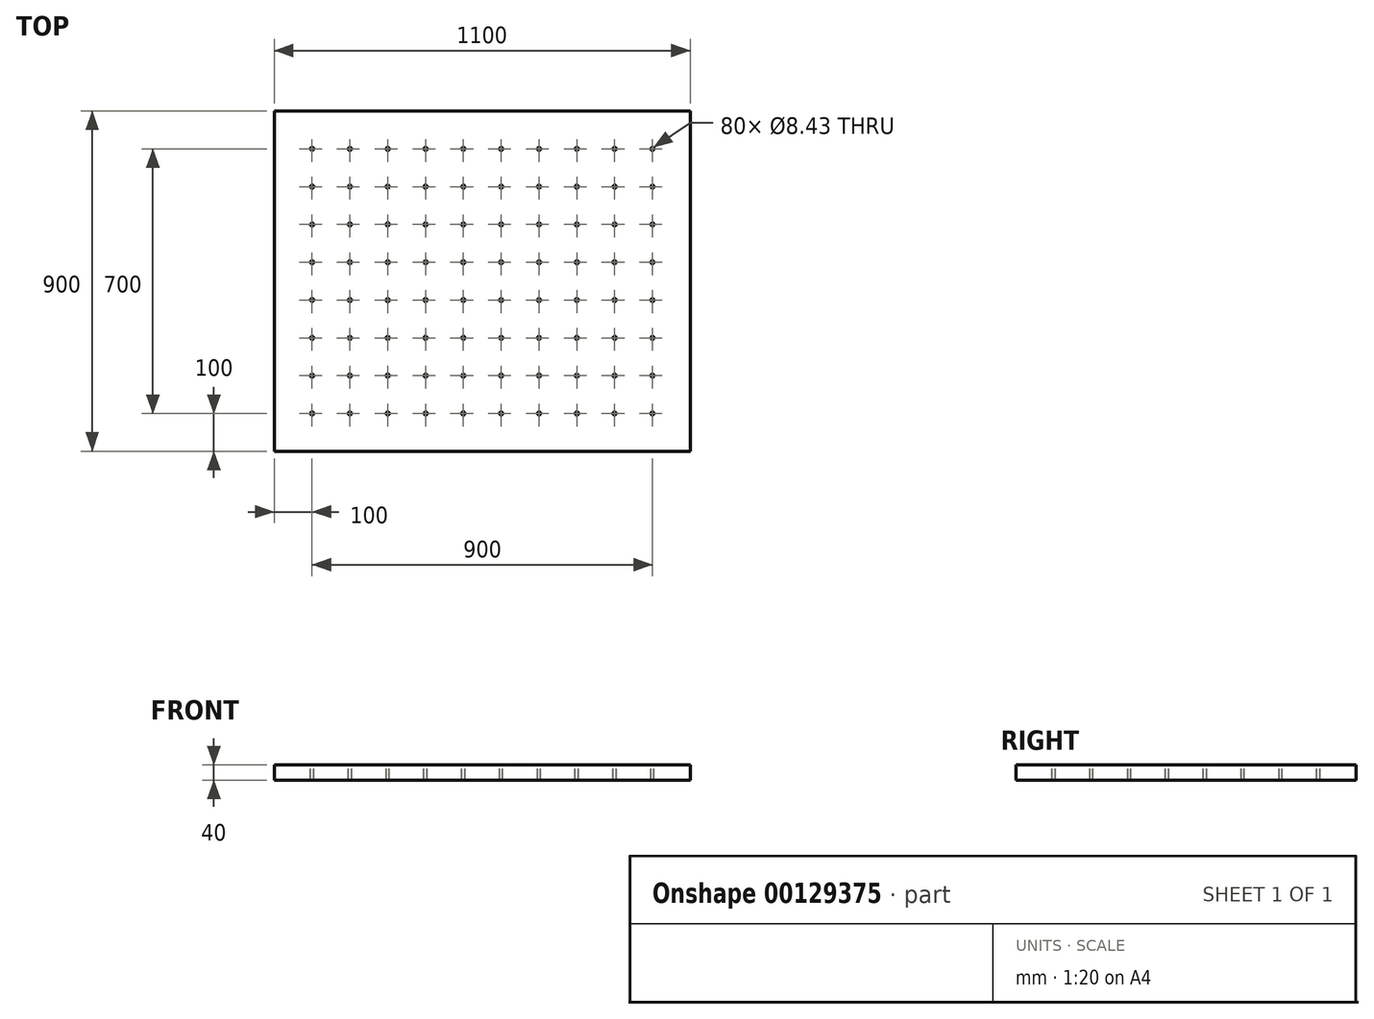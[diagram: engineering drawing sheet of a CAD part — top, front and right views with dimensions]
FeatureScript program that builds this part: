
annotation { "Feature Type Name" : "Feature", "Feature Type Description" : "" }
export const myFeature = defineFeature(function(context is Context, id is Id, definition is map)
    precondition{}
    {
        {
            var Q0;
            Q0=qCreatedBy(makeId("Top.planeOp"),FACE);
            var sketch = newSketch(context, id + "F0", { "sketchPlane" : qUnion([Q0])});
            skLineSegment(sketch, "E0.bottom", {"start": v(550, -450) * mm, "end": v(-550, -450) * mm});
            skLineSegment(sketch, "E0.top", {"start": v(550, 450) * mm, "end": v(-550, 450) * mm});
            skLineSegment(sketch, "E0.left", {"start": v(550, -450) * mm, "end": v(550, 450) * mm});
            skLineSegment(sketch, "E0.right", {"start": v(-550, -450) * mm, "end": v(-550, 450) * mm});
            skPoint(sketch, "E0.middle", {"position": v(0, 0) * mm});
            skSolve(sketch);
        }
        {
            var Q0;
            Q0=makeQuery(id+"F0.imprint","IMPRINT",FACE,{"disambiguationData":[TD([[makeQuery(id+"F0.imprint","IMPRINT",EDGE,{"derivedFrom":sQuery(id+"F0.wireOp",EDGE,"E0.bottom")}),-1.0]])]});
            extrude(context, id + "F1", {"entities" : qUnion([Q0]), "depth" : 40 * mm});
        }
        {
            var Q0;
            Q0=makeQuery(id+"F1.opExtrude","CAP_FACE",FACE,{"disambiguationData":[OSD([sQuery(id+"F0.wireOp",EDGE,"E0.bottom"),sQuery(id+"F0.wireOp",EDGE,"E0.top"),sQuery(id+"F0.wireOp",EDGE,"E0.left"),sQuery(id+"F0.wireOp",EDGE,"E0.right")])],"isStart":false});
            var sketch = newSketch(context, id + "F2", { "sketchPlane" : qUnion([Q0])});
            skPoint(sketch, "E1", {"position": v(-450, -350) * mm});
            skPoint(sketch, "E2.0.1.0", {"position": v(-450, -250) * mm});
            skPoint(sketch, "E2.0.2.0", {"position": v(-450, -150) * mm});
            skPoint(sketch, "E2.0.3.0", {"position": v(-450, -50) * mm});
            skPoint(sketch, "E2.0.4.0", {"position": v(-450, 50) * mm});
            skPoint(sketch, "E2.0.5.0", {"position": v(-450, 150) * mm});
            skPoint(sketch, "E2.0.6.0", {"position": v(-450, 250) * mm});
            skPoint(sketch, "E2.0.7.0", {"position": v(-450, 350) * mm});
            skPoint(sketch, "E2.1.0.0", {"position": v(-350, -350) * mm});
            skPoint(sketch, "E2.1.1.0", {"position": v(-350, -250) * mm});
            skPoint(sketch, "E2.1.2.0", {"position": v(-350, -150) * mm});
            skPoint(sketch, "E2.1.3.0", {"position": v(-350, -50) * mm});
            skPoint(sketch, "E2.1.4.0", {"position": v(-350, 50) * mm});
            skPoint(sketch, "E2.1.5.0", {"position": v(-350, 150) * mm});
            skPoint(sketch, "E2.1.6.0", {"position": v(-350, 250) * mm});
            skPoint(sketch, "E2.1.7.0", {"position": v(-350, 350) * mm});
            skPoint(sketch, "E2.2.0.0", {"position": v(-250, -350) * mm});
            skPoint(sketch, "E2.2.1.0", {"position": v(-250, -250) * mm});
            skPoint(sketch, "E2.2.2.0", {"position": v(-250, -150) * mm});
            skPoint(sketch, "E2.2.3.0", {"position": v(-250, -50) * mm});
            skPoint(sketch, "E2.2.4.0", {"position": v(-250, 50) * mm});
            skPoint(sketch, "E2.2.5.0", {"position": v(-250, 150) * mm});
            skPoint(sketch, "E2.2.6.0", {"position": v(-250, 250) * mm});
            skPoint(sketch, "E2.2.7.0", {"position": v(-250, 350) * mm});
            skPoint(sketch, "E2.3.0.0", {"position": v(-150, -350) * mm});
            skPoint(sketch, "E2.3.1.0", {"position": v(-150, -250) * mm});
            skPoint(sketch, "E2.3.2.0", {"position": v(-150, -150) * mm});
            skPoint(sketch, "E2.3.3.0", {"position": v(-150, -50) * mm});
            skPoint(sketch, "E2.3.4.0", {"position": v(-150, 50) * mm});
            skPoint(sketch, "E2.3.5.0", {"position": v(-150, 150) * mm});
            skPoint(sketch, "E2.3.6.0", {"position": v(-150, 250) * mm});
            skPoint(sketch, "E2.3.7.0", {"position": v(-150, 350) * mm});
            skPoint(sketch, "E2.4.0.0", {"position": v(-50, -350) * mm});
            skPoint(sketch, "E2.4.1.0", {"position": v(-50, -250) * mm});
            skPoint(sketch, "E2.4.2.0", {"position": v(-50, -150) * mm});
            skPoint(sketch, "E2.4.3.0", {"position": v(-50, -50) * mm});
            skPoint(sketch, "E2.4.4.0", {"position": v(-50, 50) * mm});
            skPoint(sketch, "E2.4.5.0", {"position": v(-50, 150) * mm});
            skPoint(sketch, "E2.4.6.0", {"position": v(-50, 250) * mm});
            skPoint(sketch, "E2.4.7.0", {"position": v(-50, 350) * mm});
            skPoint(sketch, "E2.5.0.0", {"position": v(50, -350) * mm});
            skPoint(sketch, "E2.5.1.0", {"position": v(50, -250) * mm});
            skPoint(sketch, "E2.5.2.0", {"position": v(50, -150) * mm});
            skPoint(sketch, "E2.5.3.0", {"position": v(50, -50) * mm});
            skPoint(sketch, "E2.5.4.0", {"position": v(50, 50) * mm});
            skPoint(sketch, "E2.5.5.0", {"position": v(50, 150) * mm});
            skPoint(sketch, "E2.5.6.0", {"position": v(50, 250) * mm});
            skPoint(sketch, "E2.5.7.0", {"position": v(50, 350) * mm});
            skPoint(sketch, "E2.6.0.0", {"position": v(150, -350) * mm});
            skPoint(sketch, "E2.6.1.0", {"position": v(150, -250) * mm});
            skPoint(sketch, "E2.6.2.0", {"position": v(150, -150) * mm});
            skPoint(sketch, "E2.6.3.0", {"position": v(150, -50) * mm});
            skPoint(sketch, "E2.6.4.0", {"position": v(150, 50) * mm});
            skPoint(sketch, "E2.6.5.0", {"position": v(150, 150) * mm});
            skPoint(sketch, "E2.6.6.0", {"position": v(150, 250) * mm});
            skPoint(sketch, "E2.6.7.0", {"position": v(150, 350) * mm});
            skPoint(sketch, "E2.7.0.0", {"position": v(250, -350) * mm});
            skPoint(sketch, "E2.7.1.0", {"position": v(250, -250) * mm});
            skPoint(sketch, "E2.7.2.0", {"position": v(250, -150) * mm});
            skPoint(sketch, "E2.7.3.0", {"position": v(250, -50) * mm});
            skPoint(sketch, "E2.7.4.0", {"position": v(250, 50) * mm});
            skPoint(sketch, "E2.7.5.0", {"position": v(250, 150) * mm});
            skPoint(sketch, "E2.7.6.0", {"position": v(250, 250) * mm});
            skPoint(sketch, "E2.7.7.0", {"position": v(250, 350) * mm});
            skPoint(sketch, "E2.8.0.0", {"position": v(350, -350) * mm});
            skPoint(sketch, "E2.8.1.0", {"position": v(350, -250) * mm});
            skPoint(sketch, "E2.8.2.0", {"position": v(350, -150) * mm});
            skPoint(sketch, "E2.8.3.0", {"position": v(350, -50) * mm});
            skPoint(sketch, "E2.8.4.0", {"position": v(350, 50) * mm});
            skPoint(sketch, "E2.8.5.0", {"position": v(350, 150) * mm});
            skPoint(sketch, "E2.8.6.0", {"position": v(350, 250) * mm});
            skPoint(sketch, "E2.8.7.0", {"position": v(350, 350) * mm});
            skPoint(sketch, "E2.9.0.0", {"position": v(450, -350) * mm});
            skPoint(sketch, "E2.9.1.0", {"position": v(450, -250) * mm});
            skPoint(sketch, "E2.9.2.0", {"position": v(450, -150) * mm});
            skPoint(sketch, "E2.9.3.0", {"position": v(450, -50) * mm});
            skPoint(sketch, "E2.9.4.0", {"position": v(450, 50) * mm});
            skPoint(sketch, "E2.9.5.0", {"position": v(450, 150) * mm});
            skPoint(sketch, "E2.9.6.0", {"position": v(450, 250) * mm});
            skPoint(sketch, "E2.9.7.0", {"position": v(450, 350) * mm});
            skLineSegment(sketch, "E2.direction1", {"start": v(-450, -350) * mm, "end": v(-350, -350) * mm, "construction": true});
            skLineSegment(sketch, "E2.direction2", {"start": v(-450, -350) * mm, "end": v(-450, -250) * mm, "construction": true});
            skSolve(sketch);
        }
        {
            var Q0;
            Q0=sQuery(id+"F2.wireOp",VERTEX,"E1");
            var Q1;
            Q1=sQuery(id+"F2.wireOp",VERTEX,"E2.1.0.0");
            var Q2;
            Q2=sQuery(id+"F2.wireOp",VERTEX,"E2.2.0.0");
            var Q3;
            Q3=sQuery(id+"F2.wireOp",VERTEX,"E2.0.1.0");
            var Q4;
            Q4=sQuery(id+"F2.wireOp",VERTEX,"E2.1.1.0");
            var Q5;
            Q5=sQuery(id+"F2.wireOp",VERTEX,"E2.2.1.0");
            var Q6;
            Q6=sQuery(id+"F2.wireOp",VERTEX,"E2.3.2.0");
            var Q7;
            Q7=sQuery(id+"F2.wireOp",VERTEX,"E2.4.1.0");
            var Q8;
            Q8=sQuery(id+"F2.wireOp",VERTEX,"E2.3.0.0");
            var Q9;
            Q9=sQuery(id+"F2.wireOp",VERTEX,"E2.2.2.0");
            var Q10;
            Q10=sQuery(id+"F2.wireOp",VERTEX,"E2.3.1.0");
            var Q11;
            Q11=sQuery(id+"F2.wireOp",VERTEX,"E2.8.3.0");
            var Q12;
            Q12=sQuery(id+"F2.wireOp",VERTEX,"E2.0.5.0");
            var Q13;
            Q13=sQuery(id+"F2.wireOp",VERTEX,"E2.0.3.0");
            var Q14;
            Q14=sQuery(id+"F2.wireOp",VERTEX,"E2.0.4.0");
            var Q15;
            Q15=sQuery(id+"F2.wireOp",VERTEX,"E2.0.6.0");
            var Q16;
            Q16=sQuery(id+"F2.wireOp",VERTEX,"E2.0.7.0");
            var Q17;
            Q17=sQuery(id+"F2.wireOp",VERTEX,"E2.9.4.0");
            var Q18;
            Q18=sQuery(id+"F2.wireOp",VERTEX,"E2.7.4.0");
            var Q19;
            Q19=sQuery(id+"F2.wireOp",VERTEX,"E2.5.4.0");
            var Q20;
            Q20=sQuery(id+"F2.wireOp",VERTEX,"E2.3.4.0");
            var Q21;
            Q21=sQuery(id+"F2.wireOp",VERTEX,"E2.6.7.0");
            var Q22;
            Q22=sQuery(id+"F2.wireOp",VERTEX,"E2.4.7.0");
            var Q23;
            Q23=sQuery(id+"F2.wireOp",VERTEX,"E2.2.7.0");
            var Q24;
            Q24=sQuery(id+"F2.wireOp",VERTEX,"E2.8.7.0");
            var Q25;
            Q25=sQuery(id+"F2.wireOp",VERTEX,"E2.6.5.0");
            var Q26;
            Q26=sQuery(id+"F2.wireOp",VERTEX,"E2.4.5.0");
            var Q27;
            Q27=sQuery(id+"F2.wireOp",VERTEX,"E2.2.5.0");
            var Q28;
            Q28=sQuery(id+"F2.wireOp",VERTEX,"E2.8.5.0");
            var Q29;
            Q29=sQuery(id+"F2.wireOp",VERTEX,"E2.6.3.0");
            var Q30;
            Q30=sQuery(id+"F2.wireOp",VERTEX,"E2.4.3.0");
            var Q31;
            Q31=sQuery(id+"F2.wireOp",VERTEX,"E2.2.3.0");
            var Q32;
            Q32=sQuery(id+"F2.wireOp",VERTEX,"E2.9.2.0");
            var Q33;
            Q33=sQuery(id+"F2.wireOp",VERTEX,"E2.8.1.0");
            var Q34;
            Q34=sQuery(id+"F2.wireOp",VERTEX,"E2.7.2.0");
            var Q35;
            Q35=sQuery(id+"F2.wireOp",VERTEX,"E2.6.1.0");
            var Q36;
            Q36=sQuery(id+"F2.wireOp",VERTEX,"E2.5.2.0");
            var Q37;
            Q37=sQuery(id+"F2.wireOp",VERTEX,"E2.1.7.0");
            var Q38;
            Q38=sQuery(id+"F2.wireOp",VERTEX,"E2.9.7.0");
            var Q39;
            Q39=sQuery(id+"F2.wireOp",VERTEX,"E2.7.7.0");
            var Q40;
            Q40=sQuery(id+"F2.wireOp",VERTEX,"E2.5.7.0");
            var Q41;
            Q41=sQuery(id+"F2.wireOp",VERTEX,"E2.3.7.0");
            var Q42;
            Q42=sQuery(id+"F2.wireOp",VERTEX,"E2.1.5.0");
            var Q43;
            Q43=sQuery(id+"F2.wireOp",VERTEX,"E2.9.5.0");
            var Q44;
            Q44=sQuery(id+"F2.wireOp",VERTEX,"E2.7.5.0");
            var Q45;
            Q45=sQuery(id+"F2.wireOp",VERTEX,"E2.5.5.0");
            var Q46;
            Q46=sQuery(id+"F2.wireOp",VERTEX,"E2.3.5.0");
            var Q47;
            Q47=sQuery(id+"F2.wireOp",VERTEX,"E2.7.0.0");
            var Q48;
            Q48=sQuery(id+"F2.wireOp",VERTEX,"E2.5.0.0");
            var Q49;
            Q49=sQuery(id+"F2.wireOp",VERTEX,"E2.9.0.0");
            var Q50;
            Q50=sQuery(id+"F2.wireOp",VERTEX,"E2.6.6.0");
            var Q51;
            Q51=sQuery(id+"F2.wireOp",VERTEX,"E2.4.6.0");
            var Q52;
            Q52=sQuery(id+"F2.wireOp",VERTEX,"E2.2.6.0");
            var Q53;
            Q53=sQuery(id+"F2.wireOp",VERTEX,"E2.8.6.0");
            var Q54;
            Q54=sQuery(id+"F2.wireOp",VERTEX,"E2.6.4.0");
            var Q55;
            Q55=sQuery(id+"F2.wireOp",VERTEX,"E2.4.4.0");
            var Q56;
            Q56=sQuery(id+"F2.wireOp",VERTEX,"E2.2.4.0");
            var Q57;
            Q57=sQuery(id+"F2.wireOp",VERTEX,"E2.8.4.0");
            var Q58;
            Q58=sQuery(id+"F2.wireOp",VERTEX,"E2.9.3.0");
            var Q59;
            Q59=sQuery(id+"F2.wireOp",VERTEX,"E2.7.3.0");
            var Q60;
            Q60=sQuery(id+"F2.wireOp",VERTEX,"E2.8.2.0");
            var Q61;
            Q61=sQuery(id+"F2.wireOp",VERTEX,"E2.5.3.0");
            var Q62;
            Q62=sQuery(id+"F2.wireOp",VERTEX,"E2.6.2.0");
            var Q63;
            Q63=sQuery(id+"F2.wireOp",VERTEX,"E2.3.3.0");
            var Q64;
            Q64=sQuery(id+"F2.wireOp",VERTEX,"E2.4.2.0");
            var Q65;
            Q65=sQuery(id+"F2.wireOp",VERTEX,"E2.9.1.0");
            var Q66;
            Q66=sQuery(id+"F2.wireOp",VERTEX,"E2.7.1.0");
            var Q67;
            Q67=sQuery(id+"F2.wireOp",VERTEX,"E2.8.0.0");
            var Q68;
            Q68=sQuery(id+"F2.wireOp",VERTEX,"E2.5.1.0");
            var Q69;
            Q69=sQuery(id+"F2.wireOp",VERTEX,"E2.6.0.0");
            var Q70;
            Q70=sQuery(id+"F2.wireOp",VERTEX,"E2.4.0.0");
            var Q71;
            Q71=sQuery(id+"F2.wireOp",VERTEX,"E2.1.6.0");
            var Q72;
            Q72=sQuery(id+"F2.wireOp",VERTEX,"E2.1.2.0");
            var Q73;
            Q73=sQuery(id+"F2.wireOp",VERTEX,"E2.1.3.0");
            var Q74;
            Q74=sQuery(id+"F2.wireOp",VERTEX,"E2.9.6.0");
            var Q75;
            Q75=sQuery(id+"F2.wireOp",VERTEX,"E2.7.6.0");
            var Q76;
            Q76=sQuery(id+"F2.wireOp",VERTEX,"E2.5.6.0");
            var Q77;
            Q77=sQuery(id+"F2.wireOp",VERTEX,"E2.3.6.0");
            var Q78;
            Q78=sQuery(id+"F2.wireOp",VERTEX,"E2.1.4.0");
            var Q79;
            Q79=sQuery(id+"F2.wireOp",VERTEX,"E2.0.2.0");
            var Q80;
            Q80=makeQuery(id+"F1.opExtrude","SWEPT_BODY",BODY,{"disambiguationData":[OSD([sQuery(id+"F0.wireOp",EDGE,"E0.bottom"),sQuery(id+"F0.wireOp",EDGE,"E0.top"),sQuery(id+"F0.wireOp",EDGE,"E0.left"),sQuery(id+"F0.wireOp",EDGE,"E0.right")])]});
            hole(context, id + "F3", {"style" : HoleStyle.SIMPLE, "endStyle" : HoleEndStyle.THROUGH, "standardTappedOrClearance" : lookupTablePath({ "standard" : "ANSI", "engagement" : "75%", "pitch" : "24 tpi", "size" : "3/8", "type" : "Tapped" }), "standardBlindInLast" : lookupTablePath({ "standard" : "ANSI", "engagement" : "75%", "pitch" : "24 tpi", "size" : "3/8", "type" : "Tapped" }), "holeDiameter" : 8.43 * mm, "locations" : qUnion([Q0, Q1, Q2, Q3, Q4, Q5, Q6, Q7, Q8, Q9, Q10, Q11, Q12, Q13, Q14, Q15, Q16, Q17, Q18, Q19, Q20, Q21, Q22, Q23, Q24, Q25, Q26, Q27, Q28, Q29, Q30, Q31, Q32, Q33, Q34, Q35, Q36, Q37, Q38, Q39, Q40, Q41, Q42, Q43, Q44, Q45, Q46, Q47, Q48, Q49, Q50, Q51, Q52, Q53, Q54, Q55, Q56, Q57, Q58, Q59, Q60, Q61, Q62, Q63, Q64, Q65, Q66, Q67, Q68, Q69, Q70, Q71, Q72, Q73, Q74, Q75, Q76, Q77, Q78, Q79]), "scope" : qUnion([Q80]), "isTappedThrough" : true, "majorDiameter" : 9.53 * mm, "showTappedDepth" : true});
        }
    });
